# Revit family: MOTION OLED
name_source: partatom
category: Осветительные приборы
revit_build: Autodesk Revit 2016 (Build: 20150220_1215(x64)
units: mm (PartAtom-declared; Revit-internal decimal feet)

## family parameters
Источник света = Да
Общий = Нет
Основа = Грань
При загрузке вырезать с полостями = Нет
Размер круглого соединителя = Использовать диаметр
Тип детали = Нормальный
Точка расчета площади = Нет

## types (1)
- MOTION OLED 3000K
    ADSK_Единица измерения = Шт.
    ADSK_Завод-изготовитель = ООО МГК Световые технологии
    ADSK_Код изделия = 1678000030
    ADSK_Количество фаз = 1
    ADSK_Количество фаз числовое = 1
    ADSK_Коэффициент мощности = 0.9
    ADSK_Масса = 5
    ADSK_Наименование = Подвесной светильник, создающий прямое диффузное освещение. В качестве источников света используются органические светодиоды (OLED). Корпус светильника изготовлен из искусственного камня белого цвета
    ADSK_Напряжение = 230 В
    ADSK_Номинальная мощность = 0 кВт
    ADSK_Полная мощность = 0 кВ·А
    ADSK_Размер_Ширина = 675 мм
    ADSK_Ток = 0 А
    ADSK_Энергоэффективность = 50 лм/Вт
    IP Class = IP 20
    URL = http://www.ltcompany.com
    Блок аварийного питания = Нет
    Видимая форма излучения при визуализации = Нет
    Выступ.ширина = 30 мм
    Группа модели = Светильники
    Изготовитель = ООО МГК Световые технологии
    Излучение по длине прямоугольника = 675 мм
    Излучение по ширине прямоугольника = 675 мм
    Класс Защиты = I
    Климатическая зона = УХЛ4
    Код по классификатору = D5020200
    Короб.крепление = 160 мм
    Короб.ширина = 215 мм
    Корпус = Белый металл
    Крепление.габарит = 260 мм
    Область использования = Гостиницы, Индивидуальные дома, Культурно-развлекательные, Магазины/Бутики, Объекты бытового обслуживания, Объекты общественного питания, Офисы, ТРЦ
    Описание = Подвесной светильник, создающий прямое диффузное освещение. В качестве источников света используются органические светодиоды (OLED). Корпус светильника изготовлен из искусственного камня белого цвета
    Отметка по умолчанию = 0 мм
    Плафон = Плафон самосвечение
    Полная установленная мощность = 0 кВ·А
    Разработчик = ООО ПРОРУБИМ
    Разработчик (телефон) = +7 (495) 649-85-43
    Светофильтр = 16777215
    Смещение цветовой температуры при затухании лампы = <Нет>
    Тип ИС = OLED
    Тип ПРА = Драйвер
    Тип продукции = Светильник
    Угол наклона = -90.00°
    Файл фотометрической сетки = MOTION OLED.ies

## geometry (parser evidence)
native form markers: Blend x150
no freeform markers — native parametric forms only
